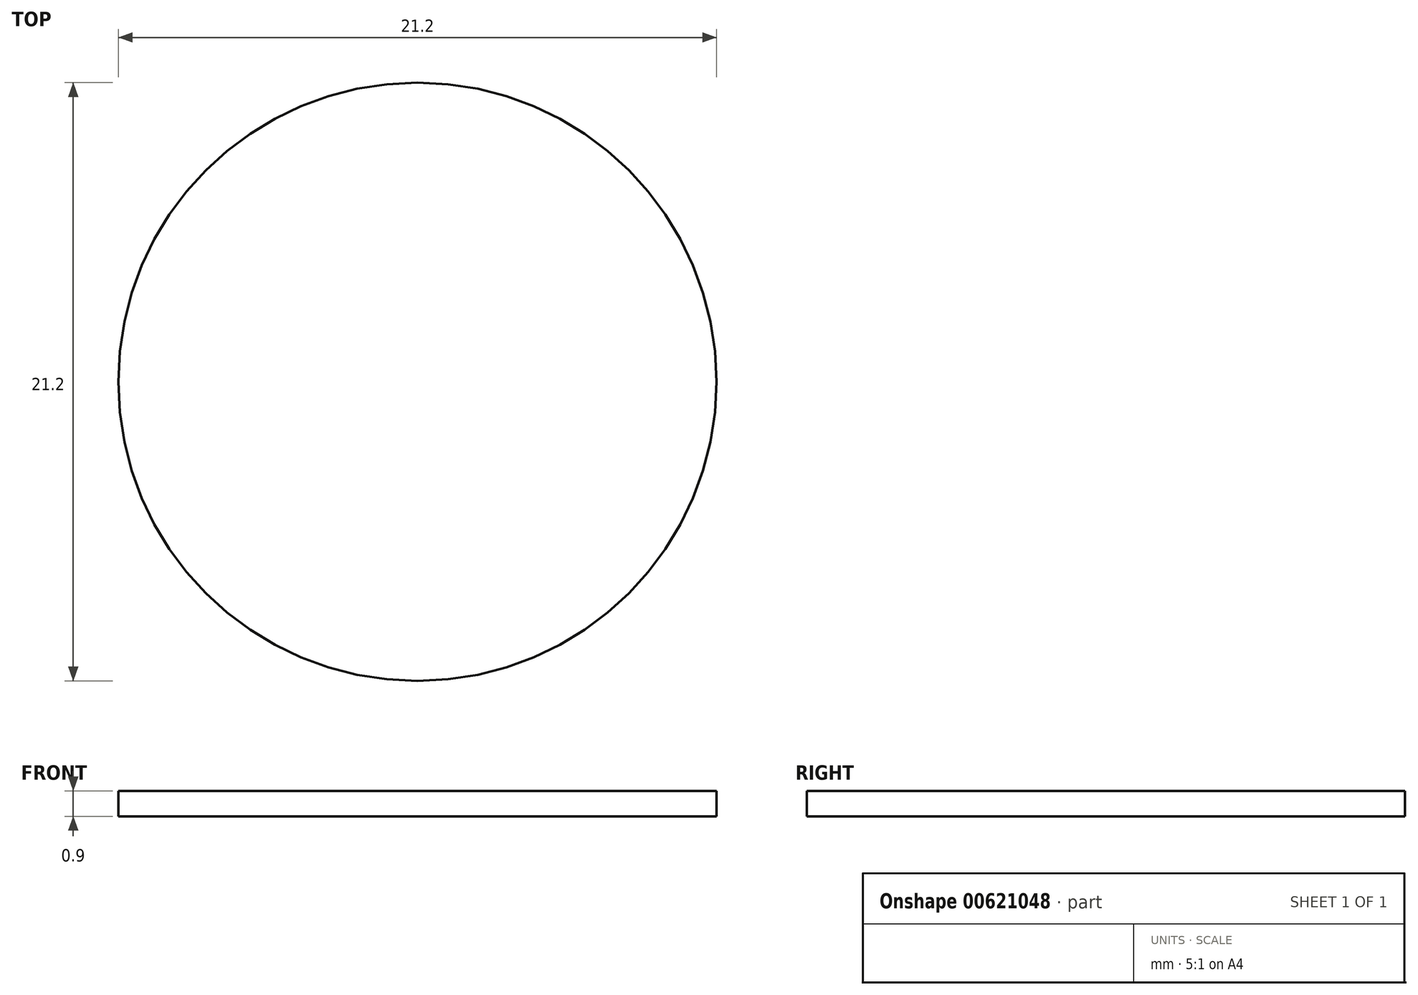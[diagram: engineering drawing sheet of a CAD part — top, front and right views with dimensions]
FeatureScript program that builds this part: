
annotation { "Feature Type Name" : "Feature", "Feature Type Description" : "" }
export const myFeature = defineFeature(function(context is Context, id is Id, definition is map)
    precondition{}
    {
        {
            var Q0;
            Q0=qCreatedBy(makeId("Top.planeOp"),FACE);
            var sketch = newSketch(context, id + "F0", { "sketchPlane" : qUnion([Q0])});
            skCircle(sketch, "E0", {"center": v(0, 0) * mm, "radius": 10.6 * mm});
            skSolve(sketch);
        }
        {
            var Q0;
            Q0=qSketchRegion(id+"F0",true);
            extrude(context, id + "F1", {"entities" : qUnion([Q0]), "depth" : .9 * mm, "offsetDistance" : 25 * mm});
        }
    });
